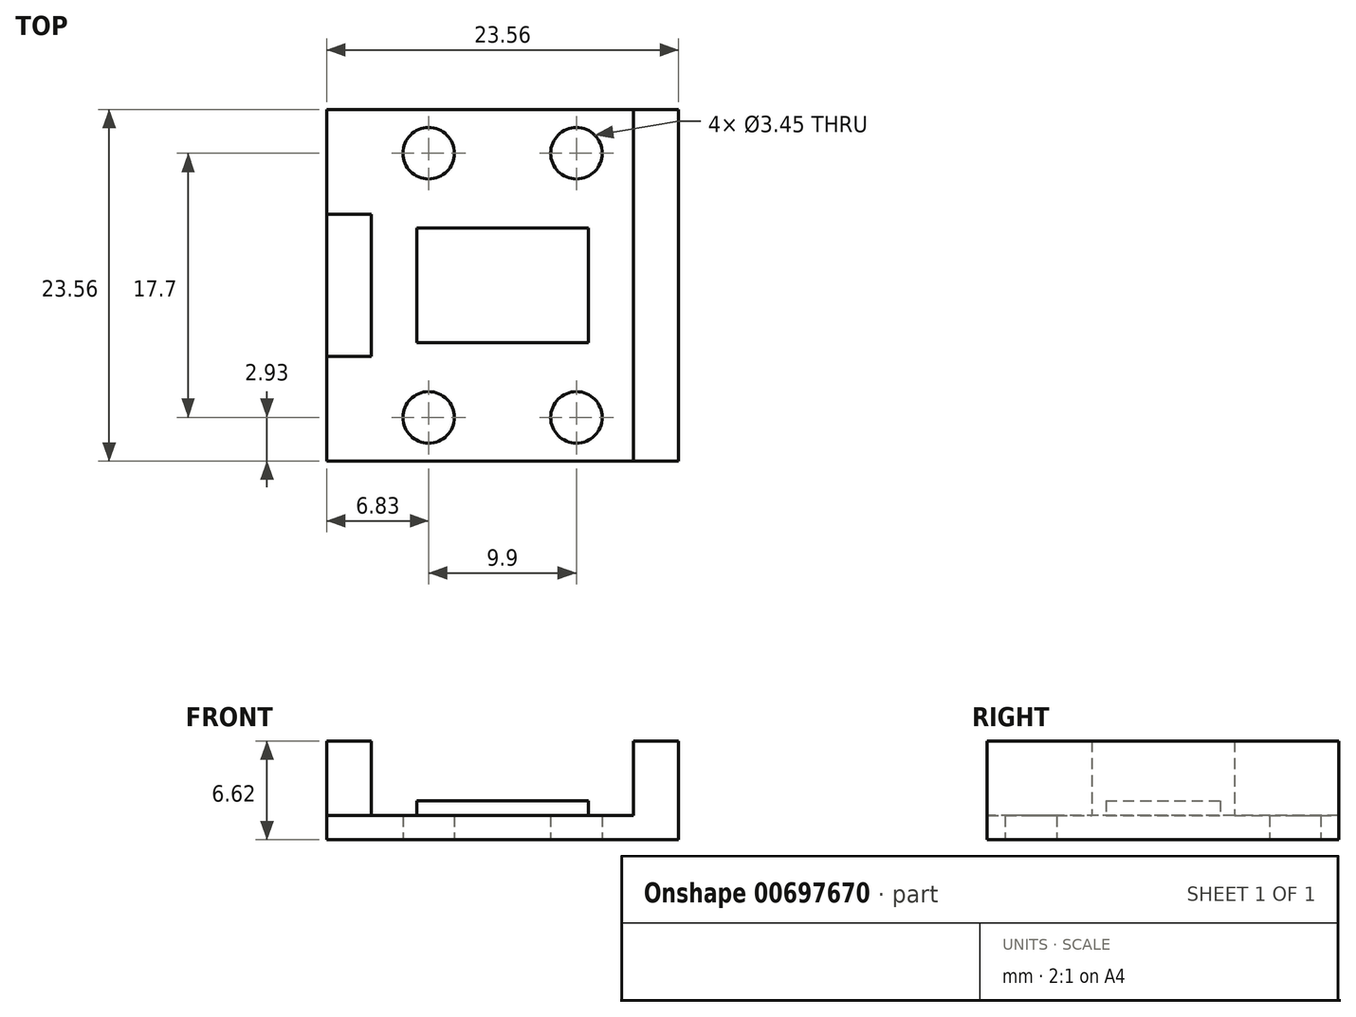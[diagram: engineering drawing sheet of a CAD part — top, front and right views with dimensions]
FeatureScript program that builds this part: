
annotation { "Feature Type Name" : "Feature", "Feature Type Description" : "" }
export const myFeature = defineFeature(function(context is Context, id is Id, definition is map)
    precondition{}
    {
        {
            var Q0;
            Q0=qCreatedBy(makeId("Top.planeOp"),FACE);
            var sketch = newSketch(context, id + "F0", { "sketchPlane" : qUnion([Q0])});
            skLineSegment(sketch, "E0.bottom", {"start": v(11.78, -11.78) * mm, "end": v(-11.77, -11.78) * mm});
            skLineSegment(sketch, "E0.top", {"start": v(11.77, 11.78) * mm, "end": v(-11.78, 11.78) * mm});
            skLineSegment(sketch, "E0.left", {"start": v(11.78, -11.78) * mm, "end": v(11.77, 11.78) * mm});
            skLineSegment(sketch, "E0.right", {"start": v(-11.77, -11.78) * mm, "end": v(-11.78, 11.78) * mm});
            skPoint(sketch, "E0.middle", {"position": v(0, 0) * mm});
            skCircle(sketch, "E1", {"center": v(-4.95, 8.85) * mm, "radius": 1.73 * mm});
            skCircle(sketch, "E2.MirrorC", {"center": v(4.95, 8.85) * mm, "radius": 1.73 * mm});
            skCircle(sketch, "E3.MirrorC", {"center": v(-4.95, -8.85) * mm, "radius": 1.73 * mm});
            skCircle(sketch, "E4.MirrorC", {"center": v(4.95, -8.85) * mm, "radius": 1.73 * mm});
            skSolve(sketch);
        }
        {
            var Q0;
            Q0=makeQuery(id+"F0.imprint","IMPRINT",FACE,{"disambiguationData":[TD([[makeQuery(id+"F0.imprint","IMPRINT",EDGE,{"derivedFrom":sQuery(id+"F0.wireOp",EDGE,"E0.bottom")}),-1.0]])]});
            extrude(context, id + "F1", {"entities" : qUnion([Q0]), "depth" : 1.62 * mm, "offsetDistance" : 25 * mm});
        }
        {
            var Q0;
            Q0=makeQuery(id+"F1.opExtrude","CAP_FACE",FACE,{"disambiguationData":[OSD([sQuery(id+"F0.wireOp",EDGE,"E0.bottom"),sQuery(id+"F0.wireOp",EDGE,"E0.top"),sQuery(id+"F0.wireOp",EDGE,"E0.left"),sQuery(id+"F0.wireOp",EDGE,"E0.right"),sQuery(id+"F0.wireOp",EDGE,"E1"),sQuery(id+"F0.wireOp",EDGE,"E2.MirrorC"),sQuery(id+"F0.wireOp",EDGE,"E3.MirrorC"),sQuery(id+"F0.wireOp",EDGE,"E4.MirrorC")])],"isStart":false});
            var sketch = newSketch(context, id + "F2", { "sketchPlane" : qUnion([Q0])});
            skLineSegment(sketch, "E5.bottom", {"start": v(-11.78, 11.78) * mm, "end": v(-8.78, 11.78) * mm});
            skLineSegment(sketch, "E5.top", {"start": v(-11.78, -11.78) * mm, "end": v(-8.78, -11.78) * mm});
            skLineSegment(sketch, "E5.left", {"start": v(-11.78, 11.78) * mm, "end": v(-11.78, -11.78) * mm});
            skLineSegment(sketch, "E5.right", {"start": v(-8.78, 11.78) * mm, "end": v(-8.78, -11.78) * mm});
            skLineSegment(sketch, "E6.MirrorCS", {"start": v(8.78, 11.78) * mm, "end": v(8.78, -11.78) * mm});
            skLineSegment(sketch, "E7.MirrorCS", {"start": v(11.78, 11.78) * mm, "end": v(8.78, 11.78) * mm});
            skLineSegment(sketch, "E8.MirrorCS", {"start": v(11.78, 11.78) * mm, "end": v(11.78, -11.78) * mm});
            skLineSegment(sketch, "E9.MirrorCS", {"start": v(11.78, -11.78) * mm, "end": v(8.78, -11.78) * mm});
            skLineSegment(sketch, "E10", {"start": v(-11.78, 4.78) * mm, "end": v(-8.78, 4.78) * mm});
            skLineSegment(sketch, "E11.MirrorCS", {"start": v(-11.78, -4.78) * mm, "end": v(-8.78, -4.78) * mm});
            skSolve(sketch);
        }
        {
            var Q0;
            Q0=makeQuery(id+"F2.imprint","IMPRINT",FACE,{"disambiguationData":[TD([[makeQuery(id+"F2.imprint","IMPRINT",EDGE,{"derivedFrom":sQuery(id+"F2.wireOp",EDGE,"E6.MirrorCS")}),1.0]])]});
            var Q1;
            {var subQ0=sQuery(id+"F2.wireOp",EDGE,"E10");Q1=makeQuery(id+"F2.imprint","IMPRINT",FACE,{"disambiguationData":[TD([[makeQuery(id+"F2.imprint","IMPRINT",EDGE,{"derivedFrom":subQ0}),-1.0]])]});}
            extrude(context, id + "F3", {"entities" : qUnion([Q0, Q1]), "operationType" : NewBodyOperationType.ADD, "depth" : 5 * mm, "offsetDistance" : 25 * mm});
        }
        {
            var Q0;
            Q0=makeQuery(id+"F1.opExtrude","CAP_FACE",FACE,{"disambiguationData":[OSD([sQuery(id+"F0.wireOp",EDGE,"E0.bottom"),sQuery(id+"F0.wireOp",EDGE,"E0.top"),sQuery(id+"F0.wireOp",EDGE,"E0.left"),sQuery(id+"F0.wireOp",EDGE,"E0.right"),sQuery(id+"F0.wireOp",EDGE,"E1"),sQuery(id+"F0.wireOp",EDGE,"E2.MirrorC"),sQuery(id+"F0.wireOp",EDGE,"E3.MirrorC"),sQuery(id+"F0.wireOp",EDGE,"E4.MirrorC")])],"isStart":false});
            var sketch = newSketch(context, id + "F4", { "sketchPlane" : qUnion([Q0])});
            skLineSegment(sketch, "E12.bottom", {"start": v(5.76, -3.83) * mm, "end": v(-5.76, -3.83) * mm});
            skLineSegment(sketch, "E12.top", {"start": v(5.76, 3.83) * mm, "end": v(-5.76, 3.83) * mm});
            skLineSegment(sketch, "E12.left", {"start": v(5.76, -3.83) * mm, "end": v(5.76, 3.83) * mm});
            skLineSegment(sketch, "E12.right", {"start": v(-5.76, -3.83) * mm, "end": v(-5.76, 3.83) * mm});
            skPoint(sketch, "E12.middle", {"position": v(0, 0) * mm});
            skSolve(sketch);
        }
        {
            var Q0;
            Q0 = qSketchRegion(id + "F4", true);
            extrude(context, id + "F5", {"entities" : qUnion([Q0]), "operationType" : NewBodyOperationType.ADD, "depth" : 1 * mm, "offsetDistance" : 25 * mm});
        }
    });
